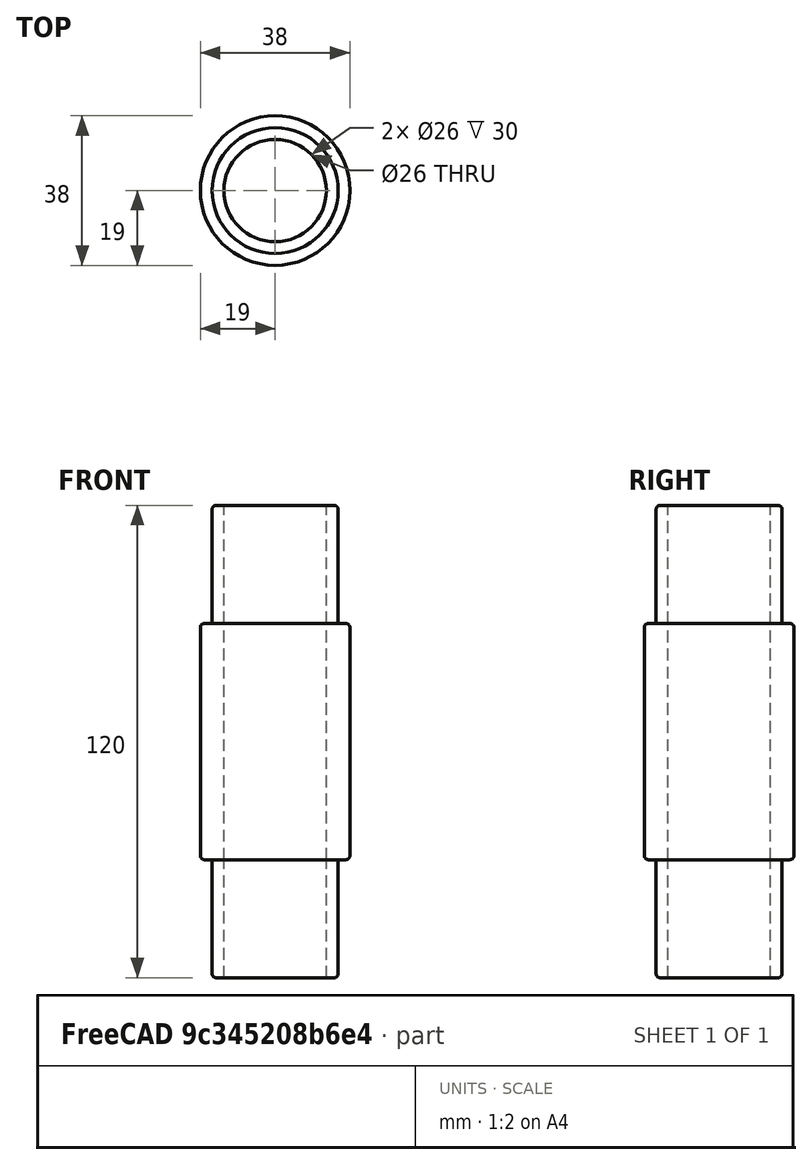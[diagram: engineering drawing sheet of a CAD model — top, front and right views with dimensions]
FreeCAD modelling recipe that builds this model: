
FCSTD DOCUMENT  (FreeCAD 0.14R2935 (Git))
Label: pool-connector-32-38mm
License: CC-BY 3.0
LicenseURL: http://creativecommons.org/licenses/by/3.0/
objects: Part::Cylinder×4, Part::Cut×2, Part::Fillet×2, Part::MultiFuse×1
note: 9 computed .brp shape members not serialized (recipe doc carries the construction recipe); baked Part::Feature solids carry a one-line shape summary decoded from their .brp

FEATURE [Part::Cylinder] Cylinder  label="Ydre 38 mm"
  Angle = 360
  Height = 60
  Placement = pos=(0,0,-30) rot=(0,0,1;0rad)
  Radius = 19
FEATURE [Part::Cylinder] Cylinder001  label="Ydre 32"
  Angle = 360
  Height = 120
  Placement = pos=(0,0,-60) rot=(0,0,1;0rad)
  Radius = 16
FEATURE [Part::Cylinder] Cylinder002  label="Indre hul"
  Angle = 360
  Height = 120
  Placement = pos=(0,0,-60) rot=(0,0,1;0rad)
  Radius = 13
FEATURE [Part::Cut] Cut
  Base = -> Cylinder001
  Tool = -> Cylinder002
FEATURE [Part::Cylinder] Cylinder003  label="Indre hul001"
  Angle = 360
  Height = 120
  Placement = pos=(0,0,-60) rot=(0,0,1;0rad)
  Radius = 13
FEATURE [Part::Cut] Cut001
  Base = -> Cylinder
  Tool = -> Cylinder003
FEATURE [Part::Fillet] Fillet
  Base = -> Cut001
  Edges = 2 edges r=1: [Edge1,Edge3]
FEATURE [Part::Fillet] Fillet001
  Base = -> Cut
  Edges = 2 edges r=1: [Edge1,Edge3]
FEATURE [Part::MultiFuse] Fusion
  Shapes = -> [Fillet,Fillet001]
